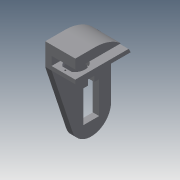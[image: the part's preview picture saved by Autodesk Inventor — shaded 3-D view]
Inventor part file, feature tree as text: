
AUTODESK INVENTOR PART (.ipt)
format: ipt  version: 2013 (Build 170138000, 138)  size: 437,248 bytes
history: native  units: mm
features: sketch x35, extrude x31
ambient origin geometry x8: Origin, YZ Plane, XZ Plane, XY Plane, X Axis, Y Axis, Z Axis, Center Point
bodies: Solid1 (feature_tree)
feature tree (66):
  extrude  "Extrusion1"  Depth=66.3mm
  extrude  "Extrusion2"  Depth=55.0mm
  extrude  "Extrusion3"  Depth=55.0mm
  extrude  "Extrusion4"  Depth=9.9mm
  extrude  "Extrusion5"  Depth=9.9mm
  extrude  "Extrusion6"  Depth=3.0mm
  extrude  "Extrusion7"  Depth=3.0mm
  extrude  "Extrusion8"  Depth=13.6mm
  extrude  "Extrusion9"  Depth=45.0mm
  sketch  "Sketch10"  dims[d22=15.0mm d23=5.0mm d24=0.0mm]
  extrude  "Extrusion10"  Depth=5.0mm TaperAngle=0.0deg
  extrude  "Extrusion11"  Depth=55.0mm
  extrude  "Extrusion12"  Depth=20.0mm
  sketch  "Sketch14"  dims[d33=10.0mm d34=32.9mm d35=0.0mm]
  extrude  "Extrusion13"  Depth=5.0mm TaperAngle=0.0deg
  extrude  "Extrusion14"  Depth=32.9mm TaperAngle=0.0deg
  extrude  "Extrusion15"  Depth=25.0mm
  extrude  "Extrusion16"  Depth=5.0mm TaperAngle=0.0deg
  extrude  "Extrusion17"  Depth=15.0mm
  sketch  "Sketch20"  dims[d50=28.0mm d51=5.0mm d52=0.0mm]
  extrude  "Extrusion18"  Depth=18.0mm
  extrude  "Extrusion19"  Depth=32.9mm TaperAngle=0.0deg
  extrude  "Extrusion20"  Depth=5.0mm TaperAngle=0.0deg
  extrude  "Extrusion21"  Depth=5.0mm
  extrude  "Extrusion22"  Depth=13.6mm
  extrude  "Extrusion23"  Depth=12.5mm
  sketch  "Sketch27"  dims[d68=21.4mm d69=2.0mm]
  extrude  "Extrusion24"  Depth=12.2mm
  extrude  "Extrusion25"  Depth=5.0mm TaperAngle=0.0deg
  extrude  "Extrusion26"  Depth=2.0mm
  extrude  "Extrusion27"  Depth=2.0mm
  sketch  "Sketch32"  dims[d80=2.05mm]
  sketch  "Sketch33"  dims[d81=2.0mm]
  extrude  "Extrusion28"  Depth=2.05mm
  extrude  "Extrusion29"  Depth=5.0mm TaperAngle=0.0deg
  extrude  "Extrusion30"  Depth=2.05mm
  extrude  "Extrusion31"  Depth=10.6mm
  sketch  "Sketch1"  dims[d0=33.15mm d2=66.3mm]
  sketch  "Sketch2"  dims[d4=18.1mm d5=55.0mm]
  sketch  "Sketch3"  dims[d6=20.0mm d7=55.0mm]
  sketch  "Sketch4"  dims[d8=40.2mm d9=9.9mm]
  sketch  "Sketch5"  dims[d10=9.5mm d11=9.9mm]
  sketch  "Sketch6"  dims[d12=9.5mm d13=3.0mm]
  sketch  "Sketch7"  dims[d14=3.0mm d15=3.0mm]
  sketch  "Sketch8"  dims[d16=3.0mm d17=13.6mm]
  sketch  "Sketch9"  dims[d20=25.0mm d21=45.0mm]
  sketch  "Sketch11"  dims[d25=18.1mm d26=55.0mm]
  sketch  "Sketch12"  dims[d27=40.2mm d28=20.0mm]
  sketch  "Sketch13"  dims[d29=5.0mm d30=0.0mm d31=5.0mm d32=0.0mm]
  sketch  "Sketch15"  dims[d36=25.0mm d37=0.0mm d38=25.0mm]
  sketch  "Sketch16"  dims[d39=10.0mm d40=5.0mm d41=0.0mm]
  sketch  "Sketch17"  dims[d42=12.5mm d43=15.0mm]
  sketch  "Sketch18"  dims[d44=10.0mm d45=0.0mm d46=18.0mm]
  sketch  "Sketch19"  dims[d47=5.0mm d48=32.9mm d49=0.0mm]
  sketch  "Sketch21"  dims[d53=10.0mm d54=0.0mm d55=5.0mm]
  sketch  "Sketch22"  dims[d56=12.5mm d57=13.6mm]
  sketch  "Sketch23"  dims[d58=10.0mm d59=0.0mm d60=12.5mm]
  sketch  "Sketch24"  dims[d61=12.4mm d62=12.2mm]
  sketch  "Sketch25"  dims[d63=6.2mm d64=5.0mm d65=0.0mm]
  sketch  "Sketch26"  dims[d66=10.6mm d67=2.0mm]
  sketch  "Sketch28"  dims[d70=5.0mm d71=0.0mm d72=2.05mm]
  sketch  "Sketch29"  dims[d73=2.05mm d74=5.0mm d75=0.0mm]
  sketch  "Sketch30"  dims[d76=21.4mm d77=2.05mm]
  sketch  "Sketch31"  dims[d78=2.0mm d79=10.6mm]
  sketch  "Sketch34"  dims[d82=5.0mm d83=0.0mm]
  sketch  "Sketch35"  dims[d84=45.0mm d86=5.0mm d87=5.0mm d88=39.0mm d89=0.0mm d90=22.0mm d91=5.0mm d92=0.0mm d93=3.0mm d94=0.0mm d95=10.0mm d96=2.0mm d97=0.0mm d98=2.0mm d99=0.0mm d100=10.25mm d101=7.25mm d102=22.0mm d103=0.0mm d104=10.0mm d105=2.0mm d106=0.0mm d107=10.0mm d108=3.0mm d109=0.0mm d111=14.0mm d112=14.0mm d113=5.0mm d114=0.0mm d115=29.9mm d116=0.0mm d117=70.0mm d118=0.0mm d119=68.0mm d120=2.0mm d121=5.0mm d122=37.9mm d123=0.0mm d124=28.0mm d125=70.0mm d126=25.0mm d127=25.0mm d128=50.0mm d129=37.9mm d130=0.0mm d131=8.0mm d132=0.0mm d133=12.0mm d134=90.0deg d135=29.9mm d136=0.0mm d137=47.0mm d138=8.0mm d139=8.0mm d140=0.0mm]
